FCSTD DOCUMENT  (FreeCAD 0.16RUnknown)
Label: 2d-box-spectro
License: All rights reserved
LicenseURL: http://en.wikipedia.org/wiki/All_rights_reserved
objects: Sketcher::SketchObject×6, Spreadsheet::Sheet×1
note: 6 computed .brp shape members not serialized (recipe doc carries the construction recipe); baked Part::Feature solids carry a one-line shape summary decoded from their .brp

FEATURE [Spreadsheet::Sheet] Spreadsheet  label="prefs"
  cells = A1=width; B1(width)==pcbLength + 2 * pcbSpace + 2 * thickness; C1=mm; A2=depth; B2(depth)==pcbWidth + 2 * pcbSpace + 2 * thickness; C2=mm; E2=surface; F2==width * depth * 3 + width * height * 2 + depth * height * 2; A3=height; B3(height)=32; C3=mm; A4=thickness; B4(thickness)=3; C4=mm; A5=space; B5(space)=5; C5=mm; D5=space between elements; A6=pcbLength; B6(pcbLength)=98.7; C6=mm; A7=pcbWidth; B7(pcbWidth)=73.2; C7=mm; A8=pcbSpace; B8(pcbSpace)=2; C8=mm; A9=supportX; B9(supportX)==pcbSpace + 3.5; C9=from box internal corner; A10=supportY; B10(supportY)==pcbSpace + 3.5; C10=from box internal corner; A11=supportRadius; B11(supportRadius)=1.5; A12=holeWidth; B12(holeWidth)=12.9; A13=holeX; B13(holeX)==48.7 + pcbSpace; C13=from box internal corner; A14=holeY; B14(holeY)==5.4 + pcbSpace; C14=from box internal corner; A15=screenLength; B15(screenLength)=71.59999999999999; A16=screenWidth; B16(screenWidth)=25.1; A17=screenX; B17(screenX)==pcbSpace + 13.4; C17=from box internal corner; A18=screenY; B18(screenY)==pcbSpace + 40.5; C18=from box internal corner; A19=rotaryX; B19(rotaryX)==pcbSpace + 13.2; A20=rotaryY; B20(rotaryY)==pcbSpace + 12.8; A21=rotaryRadius; B21(rotaryRadius)=4; A22=usbWidth; B22(usbWidth)=11; A23=usbHeight; B23(usbHeight)=9; A24=usbY; B24(usbY)==pcbSpace + 37.7; A25=usbZ; B25(usbZ)=6
FEATURE [Sketcher::SketchObject] Sketch  label="bottom"
  expr: Constraints[69] = prefs.supportY
  expr: Constraints[71] = prefs.supportY
  expr: Constraints[63] = prefs.supportRadius
  expr: Constraints[20] = prefs.depth - 2 * prefs.thickness
  expr: Constraints[70] = prefs.supportY
  expr: Constraints[22] = prefs.depth
  expr: Constraints[68] = prefs.supportY
  expr: Constraints[67] = prefs.supportX
  expr: Constraints[62] = prefs.supportRadius
  expr: Constraints[64] = prefs.supportX
  expr: Constraints[65] = prefs.supportX
  expr: Constraints[61] = prefs.supportRadius
  expr: Constraints[50] = prefs.width - 2 * prefs.thickness
  expr: Constraints[60] = prefs.supportRadius
  expr: Constraints[66] = prefs.supportX
  expr: Constraints[51] = prefs.width
  expr: Constraints[21] = prefs.depth - 2 * prefs.thickness
  sketch-geometry (25):
    g0: LineSegment StartX=3 StartY=80.2 StartZ=0 EndX=37.2333 EndY=80.2 EndZ=0
    g1: LineSegment StartX=37.2333 StartY=80.2 StartZ=0 EndX=37.2333 EndY=83.2 EndZ=0
    g2: LineSegment StartX=37.2333 StartY=83.2 StartZ=0 EndX=71.4667 EndY=83.2 EndZ=0
    g3: LineSegment StartX=71.4667 StartY=83.2 StartZ=0 EndX=71.4667 EndY=80.2 EndZ=0
    g4: LineSegment StartX=71.4667 StartY=80.2 StartZ=0 EndX=105.7 EndY=80.2 EndZ=0
    g5: LineSegment StartX=105.7 StartY=80.2 StartZ=0 EndX=105.7 EndY=54.4667 EndZ=0
    g6: LineSegment StartX=105.7 StartY=54.4667 StartZ=0 EndX=108.7 EndY=54.4667 EndZ=0
    g7: LineSegment StartX=108.7 StartY=54.4667 StartZ=0 EndX=108.7 EndY=28.7333 EndZ=0
    g8: LineSegment StartX=108.7 StartY=28.7333 StartZ=0 EndX=105.7 EndY=28.7333 EndZ=0
    g9: LineSegment StartX=105.7 StartY=28.7333 StartZ=0 EndX=105.7 EndY=3 EndZ=0
    g10: LineSegment StartX=105.7 StartY=3 StartZ=0 EndX=71.4667 EndY=3 EndZ=0
    g11: LineSegment StartX=71.4667 StartY=3 StartZ=0 EndX=71.4667 EndY=0 EndZ=0
    g12: LineSegment StartX=71.4667 StartY=0 StartZ=0 EndX=37.2333 EndY=0 EndZ=0
    g13: LineSegment StartX=37.2333 StartY=0 StartZ=0 EndX=37.2333 EndY=3 EndZ=0
    g14: LineSegment StartX=37.2333 StartY=3 StartZ=0 EndX=3 EndY=3 EndZ=0
    g15: LineSegment StartX=3 StartY=3 StartZ=0 EndX=3 EndY=28.7333 EndZ=0
    g16: LineSegment StartX=3 StartY=28.7333 StartZ=0 EndX=0 EndY=28.7333 EndZ=0
    g17: LineSegment StartX=0 StartY=28.7333 StartZ=0 EndX=0 EndY=54.4667 EndZ=0
    g18: LineSegment StartX=0 StartY=54.4667 StartZ=0 EndX=3 EndY=54.4667 EndZ=0
    g19: LineSegment StartX=3 StartY=54.4667 StartZ=0 EndX=3 EndY=80.2 EndZ=0
    g20: GeomPoint [constr] X=-41.8758 Y=-31.3252 Z=0
    g21: Circle CenterX=8.5 CenterY=74.7 CenterZ=0 NormalX=0 NormalY=0 NormalZ=1 Radius=1.5
    g22: Circle CenterX=100.2 CenterY=74.7 CenterZ=0 NormalX=0 NormalY=0 NormalZ=1 Radius=1.5
    g23: Circle CenterX=8.5 CenterY=8.5 CenterZ=0 NormalX=0 NormalY=0 NormalZ=1 Radius=1.5
    g24: Circle CenterX=100.2 CenterY=8.5 CenterZ=0 NormalX=0 NormalY=0 NormalZ=1 Radius=1.5
  constraints (72):
    c: Coincident(g0,g1)
    c: Coincident(g1,g2)
    c: Coincident(g2,g3)
    c: Coincident(g3,g4)
    c: Coincident(g4,g5)
    c: Coincident(g5,g6)
    c: Coincident(g6,g7)
    c: Coincident(g7,g8)
    c: Coincident(g8,g9)
    c: Coincident(g9,g10)
    c: Coincident(g10,g11)
    c: Coincident(g11,g12)
    c: Coincident(g12,g13)
    c: Coincident(g13,g14)
    c: Coincident(g14,g15)
    c: Coincident(g15,g16)
    c: Coincident(g16,g17)
    c: Coincident(g17,g18)
    c: Coincident(g18,g19)
    c: Coincident(g19,g0)
    c: DistanceY(g9,g4) = 77.2
    c: DistanceY(g14,g0) = 77.2
    c: DistanceY(g12,g1) = 83.2
    c: Horizontal(g0)
    c: Horizontal(g2)
    c: Horizontal(g4)
    c: Horizontal(g10)
    c: Horizontal(g12)
    c: Horizontal(g14)
    c: Equal(g1,g13)
    c: Equal(g0,g2)
    c: Equal(g2,g4)
    c: Equal(g4,g10)
    c: Equal(g10,g12)
    c: Equal(g12,g14)
    c: Equal(g3,g11)
    c: Equal(g5,g7)
    c: Equal(g7,g9)
    c: Equal(g9,g19)
    c: Equal(g19,g17)
    c: Equal(g17,g15)
    c: Vertical(g3)
    c: Vertical(g1)
    c: Vertical(g13)
    c: Vertical(g11)
    c: Horizontal(g18)
    c: Horizontal(g16)
    c: Horizontal(g8)
    c: Equal(g18,g6)
    c: Equal(g16,g8)
    c: DistanceX(g0,g4) = 102.7
    c: DistanceX(g16,g7) = 108.7
    c: Vertical(g15)
    c: Vertical(g19)
    c: Vertical(g17)
    c: Vertical(g5)
    c: Vertical(g7)
    c: Vertical(g9)
    c: DistanceX(g-1,g16) = 0
    c: DistanceY(g12,g-1) = 0
    c: Radius(g21) = 1.5
    c: Radius(g22) = 1.5
    c: Radius(g23) = 1.5
    c: Radius(g24) = 1.5
    c: DistanceX(g0,g21) = 5.5
    c: DistanceX(g22,g4) = 5.5
    c: DistanceX(g24,g9) = 5.5
    c: DistanceX(g14,g23) = 5.5
    c: DistanceY(g21,g0) = 5.5
    c: DistanceY(g22,g4) = 5.5
    c: DistanceY(g9,g24) = 5.5
    c: DistanceY(g14,g23) = 5.5
FEATURE [Sketcher::SketchObject] Sketch001  label="front"
  Placement = pos=(0,88.2,0) rot=(0,0,1;0rad)
  expr: Placement.Base.y = prefs.depth + Spreadsheet.space
  expr: Constraints[20] = prefs.height
  expr: Constraints[49] = prefs.width
  expr: Constraints[21] = prefs.height
  expr: Constraints[48] = prefs.width - 2 * prefs.thickness
  expr: Constraints[22] = prefs.height - 2 * prefs.thickness
  sketch-geometry (21):
    g0: LineSegment StartX=3 StartY=32 StartZ=0 EndX=37.2333 EndY=32 EndZ=0
    g1: LineSegment StartX=37.2333 StartY=32 StartZ=0 EndX=37.2333 EndY=29 EndZ=0
    g2: LineSegment StartX=37.2333 StartY=29 StartZ=0 EndX=71.4667 EndY=29 EndZ=0
    g3: LineSegment StartX=71.4667 StartY=29 StartZ=0 EndX=71.4667 EndY=32 EndZ=0
    g4: LineSegment StartX=71.4667 StartY=32 StartZ=0 EndX=105.7 EndY=32 EndZ=0
    g5: LineSegment StartX=105.7 StartY=32 StartZ=0 EndX=105.7 EndY=21.3333 EndZ=0
    g6: LineSegment StartX=105.7 StartY=21.3333 StartZ=0 EndX=108.7 EndY=21.3333 EndZ=0
    g7: LineSegment StartX=108.7 StartY=21.3333 StartZ=0 EndX=108.7 EndY=10.6667 EndZ=0
    g8: LineSegment StartX=108.7 StartY=10.6667 StartZ=0 EndX=105.7 EndY=10.6667 EndZ=0
    g9: LineSegment StartX=105.7 StartY=10.6667 StartZ=0 EndX=105.7 EndY=0 EndZ=0
    g10: LineSegment StartX=105.7 StartY=0 StartZ=0 EndX=71.4667 EndY=0 EndZ=0
    g11: LineSegment StartX=71.4667 StartY=0 StartZ=0 EndX=71.4667 EndY=3 EndZ=0
    g12: LineSegment StartX=71.4667 StartY=3 StartZ=0 EndX=37.2333 EndY=3 EndZ=0
    g13: LineSegment StartX=37.2333 StartY=3 StartZ=0 EndX=37.2333 EndY=0 EndZ=0
    g14: LineSegment StartX=37.2333 StartY=0 StartZ=0 EndX=3 EndY=0 EndZ=0
    g15: LineSegment StartX=3 StartY=0 StartZ=0 EndX=3 EndY=10.6667 EndZ=0
    g16: LineSegment StartX=3 StartY=10.6667 StartZ=0 EndX=0 EndY=10.6667 EndZ=0
    g17: LineSegment StartX=0 StartY=10.6667 StartZ=0 EndX=0 EndY=21.3333 EndZ=0
    g18: LineSegment StartX=0 StartY=21.3333 StartZ=0 EndX=3 EndY=21.3333 EndZ=0
    g19: LineSegment StartX=3 StartY=21.3333 StartZ=0 EndX=3 EndY=32 EndZ=0
    g20: GeomPoint [constr] X=-41.8758 Y=-31.3252 Z=0
  constraints (60):
    c: Coincident(g0,g1)
    c: Coincident(g1,g2)
    c: Coincident(g2,g3)
    c: Coincident(g3,g4)
    c: Coincident(g4,g5)
    c: Coincident(g5,g6)
    c: Coincident(g6,g7)
    c: Coincident(g7,g8)
    c: Coincident(g8,g9)
    c: Coincident(g9,g10)
    c: Coincident(g10,g11)
    c: Coincident(g11,g12)
    c: Coincident(g12,g13)
    c: Coincident(g13,g14)
    c: Coincident(g14,g15)
    c: Coincident(g15,g16)
    c: Coincident(g16,g17)
    c: Coincident(g17,g18)
    c: Coincident(g18,g19)
    c: Coincident(g19,g0)
    c: DistanceY(g9,g4) = 32
    c: DistanceY(g14,g0) = 32
    c: DistanceY(g12,g1) = 26
    c: Horizontal(g0)
    c: Horizontal(g2)
    c: Horizontal(g4)
    c: Horizontal(g10)
    c: Horizontal(g12)
    c: Horizontal(g14)
    c: Equal(g0,g2)
    c: Equal(g2,g4)
    c: Equal(g4,g10)
    c: Equal(g10,g12)
    c: Equal(g12,g14)
    c: Equal(g5,g7)
    c: Equal(g7,g9)
    c: Equal(g9,g19)
    c: Equal(g19,g17)
    c: Equal(g17,g15)
    c: Vertical(g3)
    c: Vertical(g1)
    c: Vertical(g13)
    c: Vertical(g11)
    c: Horizontal(g18)
    c: Horizontal(g16)
    c: Horizontal(g8)
    c: Equal(g18,g6)
    c: Equal(g16,g8)
    c: DistanceX(g0,g4) = 102.7
    c: DistanceX(g16,g7) = 108.7
    c: Vertical(g15)
    c: Vertical(g19)
    c: Vertical(g17)
    c: Vertical(g5)
    c: Vertical(g7)
    c: Vertical(g9)
    c: DistanceX(g-1,g16) = 0
    c: Equal(g1,g13)
    c: Equal(g3,g11)
    c: DistanceY(g-1,g14) = 0
FEATURE [Sketcher::SketchObject] Sketch002  label="left"
  Placement = pos=(0,125.2,0) rot=(0,0,1;0rad)
  expr: Constraints[59] = (prefs.depth - 2 * prefs.thickness) / 3
  expr: Constraints[53] = prefs.depth - 2 * prefs.thickness
  expr: Constraints[54] = prefs.depth
  expr: Placement.Base.y = prefs.depth + prefs.height + Spreadsheet.space * 2
  expr: Constraints[20] = prefs.height
  expr: Constraints[21] = prefs.height
  expr: Constraints[22] = prefs.height - 2 * prefs.thickness
  sketch-geometry (21):
    g0: LineSegment StartX=0 StartY=32 StartZ=0 EndX=28.7333 EndY=32 EndZ=0
    g1: LineSegment StartX=28.7333 StartY=32 StartZ=0 EndX=28.7333 EndY=29 EndZ=0
    g2: LineSegment StartX=28.7333 StartY=29 StartZ=0 EndX=54.4667 EndY=29 EndZ=0
    g3: LineSegment StartX=54.4667 StartY=29 StartZ=0 EndX=54.4667 EndY=32 EndZ=0
    g4: LineSegment StartX=54.4667 StartY=32 StartZ=0 EndX=83.2 EndY=32 EndZ=0
    g5: LineSegment StartX=83.2 StartY=32 StartZ=0 EndX=83.2 EndY=21.3333 EndZ=0
    g6: LineSegment StartX=83.2 StartY=21.3333 StartZ=0 EndX=80.2 EndY=21.3333 EndZ=0
    g7: LineSegment StartX=80.2 StartY=21.3333 StartZ=0 EndX=80.2 EndY=10.6667 EndZ=0
    g8: LineSegment StartX=80.2 StartY=10.6667 StartZ=0 EndX=83.2 EndY=10.6667 EndZ=0
    g9: LineSegment StartX=83.2 StartY=10.6667 StartZ=0 EndX=83.2 EndY=0 EndZ=0
    g10: LineSegment StartX=83.2 StartY=0 StartZ=0 EndX=54.4667 EndY=0 EndZ=0
    g11: LineSegment StartX=54.4667 StartY=0 StartZ=0 EndX=54.4667 EndY=3 EndZ=0
    g12: LineSegment StartX=54.4667 StartY=3 StartZ=0 EndX=28.7333 EndY=3 EndZ=0
    g13: LineSegment StartX=28.7333 StartY=3 StartZ=0 EndX=28.7333 EndY=0 EndZ=0
    g14: LineSegment StartX=28.7333 StartY=0 StartZ=0 EndX=0 EndY=0 EndZ=0
    g15: LineSegment StartX=0 StartY=0 StartZ=0 EndX=0 EndY=10.6667 EndZ=0
    g16: LineSegment StartX=0 StartY=10.6667 StartZ=0 EndX=3 EndY=10.6667 EndZ=0
    g17: LineSegment StartX=3 StartY=10.6667 StartZ=0 EndX=3 EndY=21.3333 EndZ=0
    g18: LineSegment StartX=3 StartY=21.3333 StartZ=0 EndX=0 EndY=21.3333 EndZ=0
    g19: LineSegment StartX=0 StartY=21.3333 StartZ=0 EndX=0 EndY=32 EndZ=0
    g20: GeomPoint [constr] X=-41.8758 Y=-31.3252 Z=0
  constraints (60):
    c: Coincident(g0,g1)
    c: Coincident(g1,g2)
    c: Coincident(g2,g3)
    c: Coincident(g3,g4)
    c: Coincident(g4,g5)
    c: Coincident(g5,g6)
    c: Coincident(g6,g7)
    c: Coincident(g7,g8)
    c: Coincident(g8,g9)
    c: Coincident(g9,g10)
    c: Coincident(g10,g11)
    c: Coincident(g11,g12)
    c: Coincident(g12,g13)
    c: Coincident(g13,g14)
    c: Coincident(g14,g15)
    c: Coincident(g15,g16)
    c: Coincident(g16,g17)
    c: Coincident(g17,g18)
    c: Coincident(g18,g19)
    c: Coincident(g19,g0)
    c: DistanceY(g9,g4) = 32
    c: DistanceY(g14,g0) = 32
    c: DistanceY(g12,g1) = 26
    c: Horizontal(g0)
    c: Horizontal(g2)
    c: Horizontal(g4)
    c: Horizontal(g10)
    c: Horizontal(g12)
    c: Horizontal(g14)
    c: Equal(g4,g10)
    c: Equal(g5,g7)
    c: Equal(g7,g9)
    c: Equal(g9,g19)
    c: Equal(g19,g17)
    c: Equal(g17,g15)
    c: Vertical(g3)
    c: Vertical(g1)
    c: Vertical(g13)
    c: Vertical(g11)
    c: Horizontal(g18)
    c: Horizontal(g16)
    c: Vertical(g15)
    c: Vertical(g19)
    c: Vertical(g17)
    c: Vertical(g5)
    c: Vertical(g7)
    c: Vertical(g9)
    c: Equal(g1,g13)
    c: Equal(g3,g11)
    c: DistanceY(g-1,g14) = 0
    c: Horizontal(g6)
    c: Equal(g18,g6)
    c: Equal(g16,g8)
    c: DistanceX(g17,g6) = 77.2
    c: DistanceX(g0,g4) = 83.2
    c: DistanceX(g-1,g14) = 0
    c: Equal(g14,g10)
    c: Equal(g0,g4)
    c: Equal(g2,g12)
    c: DistanceX(g2,g2) = 25.7333
FEATURE [Sketcher::SketchObject] Sketch003  label="top"
  Placement = pos=(113.7,0,0) rot=(0,0,1;0rad)
  expr: Constraints[87] = prefs.supportX
  expr: Constraints[79] = prefs.supportRadius
  expr: Constraints[93] = prefs.holeWidth
  expr: Constraints[92] = prefs.rotaryRadius
  expr: Constraints[77] = prefs.supportRadius
  expr: Constraints[98] = prefs.screenX
  expr: Constraints[95] = prefs.holeY
  expr: Constraints[89] = prefs.screenWidth
  expr: Constraints[84] = prefs.supportX
  expr: Constraints[76] = prefs.supportRadius
  expr: Constraints[22] = prefs.depth
  expr: Constraints[50] = prefs.width - 2 * prefs.thickness
  expr: Constraints[96] = prefs.holeX
  expr: Constraints[97] = prefs.rotaryX
  expr: Constraints[82] = prefs.supportX
  expr: Constraints[86] = prefs.supportY
  expr: Constraints[88] = prefs.screenLength
  expr: Placement.Base.x = prefs.width + Spreadsheet.space
  expr: Constraints[85] = prefs.supportY
  expr: Constraints[83] = prefs.supportY
  expr: Constraints[78] = prefs.supportRadius
  expr: Constraints[81] = prefs.supportY
  expr: Constraints[21] = prefs.depth - 2 * prefs.thickness
  expr: Constraints[51] = prefs.width
  expr: Constraints[20] = prefs.depth - 2 * prefs.thickness
  expr: Constraints[80] = prefs.supportX
  sketch-geometry (34):
    g0: LineSegment StartX=3 StartY=80.2 StartZ=0 EndX=37.2333 EndY=80.2 EndZ=0
    g1: LineSegment StartX=37.2333 StartY=80.2 StartZ=0 EndX=37.2333 EndY=83.2 EndZ=0
    g2: LineSegment StartX=37.2333 StartY=83.2 StartZ=0 EndX=71.4667 EndY=83.2 EndZ=0
    g3: LineSegment StartX=71.4667 StartY=83.2 StartZ=0 EndX=71.4667 EndY=80.2 EndZ=0
    g4: LineSegment StartX=71.4667 StartY=80.2 StartZ=0 EndX=105.7 EndY=80.2 EndZ=0
    g5: LineSegment StartX=105.7 StartY=80.2 StartZ=0 EndX=105.7 EndY=54.4667 EndZ=0
    g6: LineSegment StartX=105.7 StartY=54.4667 StartZ=0 EndX=108.7 EndY=54.4667 EndZ=0
    g7: LineSegment StartX=108.7 StartY=54.4667 StartZ=0 EndX=108.7 EndY=28.7333 EndZ=0
    g8: LineSegment StartX=108.7 StartY=28.7333 StartZ=0 EndX=105.7 EndY=28.7333 EndZ=0
    g9: LineSegment StartX=105.7 StartY=28.7333 StartZ=0 EndX=105.7 EndY=3 EndZ=0
    g10: LineSegment StartX=105.7 StartY=3 StartZ=0 EndX=71.4667 EndY=3 EndZ=0
    g11: LineSegment StartX=71.4667 StartY=3 StartZ=0 EndX=71.4667 EndY=0 EndZ=0
    g12: LineSegment StartX=71.4667 StartY=0 StartZ=0 EndX=37.2333 EndY=0 EndZ=0
    g13: LineSegment StartX=37.2333 StartY=0 StartZ=0 EndX=37.2333 EndY=3 EndZ=0
    g14: LineSegment StartX=37.2333 StartY=3 StartZ=0 EndX=3 EndY=3 EndZ=0
    g15: LineSegment StartX=3 StartY=3 StartZ=0 EndX=3 EndY=28.7333 EndZ=0
    g16: LineSegment StartX=3 StartY=28.7333 StartZ=0 EndX=0 EndY=28.7333 EndZ=0
    g17: LineSegment StartX=0 StartY=28.7333 StartZ=0 EndX=0 EndY=54.4667 EndZ=0
    g18: LineSegment StartX=0 StartY=54.4667 StartZ=0 EndX=3 EndY=54.4667 EndZ=0
    g19: LineSegment StartX=3 StartY=54.4667 StartZ=0 EndX=3 EndY=80.2 EndZ=0
    g20: GeomPoint [constr] X=-41.8758 Y=-31.3252 Z=0
    g21: LineSegment StartX=18.7 StartY=69.1 StartZ=0 EndX=90.3 EndY=69.1 EndZ=0
    g22: LineSegment StartX=90.3 StartY=69.1 StartZ=0 EndX=90.3 EndY=44 EndZ=0
    g23: LineSegment StartX=90.3 StartY=44 StartZ=0 EndX=18.7 EndY=44 EndZ=0
    g24: LineSegment StartX=18.7 StartY=44 StartZ=0 EndX=18.7 EndY=69.1 EndZ=0
    g25: Circle CenterX=90.5 CenterY=16.3 CenterZ=0 NormalX=0 NormalY=0 NormalZ=1 Radius=4
    g26: Circle CenterX=8.5 CenterY=74.7 CenterZ=0 NormalX=0 NormalY=0 NormalZ=1 Radius=1.5
    g27: Circle CenterX=100.2 CenterY=74.7 CenterZ=0 NormalX=0 NormalY=0 NormalZ=1 Radius=1.5
    g28: Circle CenterX=8.5 CenterY=8.5 CenterZ=0 NormalX=0 NormalY=0 NormalZ=1 Radius=1.5
    g29: Circle CenterX=100.2 CenterY=8.5 CenterZ=0 NormalX=0 NormalY=0 NormalZ=1 Radius=1.5
    g30: LineSegment StartX=42.1 StartY=23.3 StartZ=0 EndX=55 EndY=23.3 EndZ=0
    g31: LineSegment StartX=55 StartY=23.3 StartZ=0 EndX=55 EndY=10.4 EndZ=0
    g32: LineSegment StartX=55 StartY=10.4 StartZ=0 EndX=42.1 EndY=10.4 EndZ=0
    g33: LineSegment StartX=42.1 StartY=10.4 StartZ=0 EndX=42.1 EndY=23.3 EndZ=0
  constraints (99):
    c: Coincident(g0,g1)
    c: Coincident(g1,g2)
    c: Coincident(g2,g3)
    c: Coincident(g3,g4)
    c: Coincident(g4,g5)
    c: Coincident(g5,g6)
    c: Coincident(g6,g7)
    c: Coincident(g7,g8)
    c: Coincident(g8,g9)
    c: Coincident(g9,g10)
    c: Coincident(g10,g11)
    c: Coincident(g11,g12)
    c: Coincident(g12,g13)
    c: Coincident(g13,g14)
    c: Coincident(g14,g15)
    c: Coincident(g15,g16)
    c: Coincident(g16,g17)
    c: Coincident(g17,g18)
    c: Coincident(g18,g19)
    c: Coincident(g19,g0)
    c: DistanceY(g9,g4) = 77.2
    c: DistanceY(g14,g0) = 77.2
    c: DistanceY(g12,g1) = 83.2
    c: Horizontal(g0)
    c: Horizontal(g2)
    c: Horizontal(g4)
    c: Horizontal(g10)
    c: Horizontal(g12)
    c: Horizontal(g14)
    c: Equal(g1,g13)
    c: Equal(g0,g2)
    c: Equal(g2,g4)
    c: Equal(g4,g10)
    c: Equal(g10,g12)
    c: Equal(g12,g14)
    c: Equal(g3,g11)
    c: Equal(g5,g7)
    c: Equal(g7,g9)
    c: Equal(g9,g19)
    c: Equal(g19,g17)
    c: Equal(g17,g15)
    c: Vertical(g3)
    c: Vertical(g1)
    c: Vertical(g13)
    c: Vertical(g11)
    c: Horizontal(g18)
    c: Horizontal(g16)
    c: Horizontal(g8)
    c: Equal(g18,g6)
    c: Equal(g16,g8)
    c: DistanceX(g0,g4) = 102.7
    c: DistanceX(g16,g7) = 108.7
    c: Vertical(g15)
    c: Vertical(g19)
    c: Vertical(g17)
    c: Vertical(g5)
    c: Vertical(g7)
    c: Vertical(g9)
    c: DistanceX(g-1,g16) = 0
    c: DistanceY(g12,g-1) = 0
    c: Coincident(g21,g22)
    c: Coincident(g22,g23)
    c: Coincident(g23,g24)
    c: Coincident(g24,g21)
    c: Horizontal(g21)
    c: Horizontal(g23)
    c: Vertical(g22)
    c: Vertical(g24)
    c: Coincident(g30,g31)
    c: Coincident(g31,g32)
    c: Coincident(g32,g33)
    c: Coincident(g33,g30)
    c: Horizontal(g30)
    c: Horizontal(g32)
    c: Vertical(g31)
    c: Vertical(g33)
    c: Radius(g26) = 1.5
    c: Radius(g28) = 1.5
    c: Radius(g27) = 1.5
    c: Radius(g29) = 1.5
    c: DistanceX(g0,g26) = 5.5
    c: DistanceY(g26,g0) = 5.5
    c: DistanceX(g27,g4) = 5.5
    c: DistanceY(g27,g4) = 5.5
    c: DistanceX(g29,g9) = 5.5
    c: DistanceY(g9,g29) = 5.5
    c: DistanceY(g14,g28) = 5.5
    c: DistanceX(g14,g28) = 5.5
    c: DistanceX(g23,g22) = 71.6
    c: DistanceY(g22,g21) = 25.1
    c: DistanceY(g14,g23) = 41
    c: DistanceY(g14,g25) = 13.3
    c: Radius(g25) = 4
    c: DistanceX(g30,g30) = 12.9
    c: Equal(g30,g31)
    c: DistanceY(g14,g32) = 7.4
    c: DistanceX(g31,g9) = 50.7
    c: DistanceX(g25,g9) = 15.2
    c: DistanceX(g22,g9) = 15.4
FEATURE [Sketcher::SketchObject] Sketch004  label="back"
  Placement = pos=(113.7,88.2,0) rot=(0,0,1;0rad)
  expr: Placement.Base.x = prefs.width + Spreadsheet.space
  expr: Placement.Base.y = prefs.depth + Spreadsheet.space
  expr: Constraints[20] = prefs.height
  expr: Constraints[49] = prefs.width
  expr: Constraints[21] = prefs.height
  expr: Constraints[48] = prefs.width - 2 * prefs.thickness
  expr: Constraints[22] = prefs.height - 2 * prefs.thickness
  sketch-geometry (21):
    g0: LineSegment StartX=3 StartY=32 StartZ=0 EndX=37.2333 EndY=32 EndZ=0
    g1: LineSegment StartX=37.2333 StartY=32 StartZ=0 EndX=37.2333 EndY=29 EndZ=0
    g2: LineSegment StartX=37.2333 StartY=29 StartZ=0 EndX=71.4667 EndY=29 EndZ=0
    g3: LineSegment StartX=71.4667 StartY=29 StartZ=0 EndX=71.4667 EndY=32 EndZ=0
    g4: LineSegment StartX=71.4667 StartY=32 StartZ=0 EndX=105.7 EndY=32 EndZ=0
    g5: LineSegment StartX=105.7 StartY=32 StartZ=0 EndX=105.7 EndY=21.3333 EndZ=0
    g6: LineSegment StartX=105.7 StartY=21.3333 StartZ=0 EndX=108.7 EndY=21.3333 EndZ=0
    g7: LineSegment StartX=108.7 StartY=21.3333 StartZ=0 EndX=108.7 EndY=10.6667 EndZ=0
    g8: LineSegment StartX=108.7 StartY=10.6667 StartZ=0 EndX=105.7 EndY=10.6667 EndZ=0
    g9: LineSegment StartX=105.7 StartY=10.6667 StartZ=0 EndX=105.7 EndY=0 EndZ=0
    g10: LineSegment StartX=105.7 StartY=0 StartZ=0 EndX=71.4667 EndY=0 EndZ=0
    g11: LineSegment StartX=71.4667 StartY=0 StartZ=0 EndX=71.4667 EndY=3 EndZ=0
    g12: LineSegment StartX=71.4667 StartY=3 StartZ=0 EndX=37.2333 EndY=3 EndZ=0
    g13: LineSegment StartX=37.2333 StartY=3 StartZ=0 EndX=37.2333 EndY=0 EndZ=0
    g14: LineSegment StartX=37.2333 StartY=0 StartZ=0 EndX=3 EndY=0 EndZ=0
    g15: LineSegment StartX=3 StartY=0 StartZ=0 EndX=3 EndY=10.6667 EndZ=0
    g16: LineSegment StartX=3 StartY=10.6667 StartZ=0 EndX=0 EndY=10.6667 EndZ=0
    g17: LineSegment StartX=0 StartY=10.6667 StartZ=0 EndX=0 EndY=21.3333 EndZ=0
    g18: LineSegment StartX=0 StartY=21.3333 StartZ=0 EndX=3 EndY=21.3333 EndZ=0
    g19: LineSegment StartX=3 StartY=21.3333 StartZ=0 EndX=3 EndY=32 EndZ=0
    g20: GeomPoint [constr] X=-41.8758 Y=-31.3252 Z=0
  constraints (60):
    c: Coincident(g0,g1)
    c: Coincident(g1,g2)
    c: Coincident(g2,g3)
    c: Coincident(g3,g4)
    c: Coincident(g4,g5)
    c: Coincident(g5,g6)
    c: Coincident(g6,g7)
    c: Coincident(g7,g8)
    c: Coincident(g8,g9)
    c: Coincident(g9,g10)
    c: Coincident(g10,g11)
    c: Coincident(g11,g12)
    c: Coincident(g12,g13)
    c: Coincident(g13,g14)
    c: Coincident(g14,g15)
    c: Coincident(g15,g16)
    c: Coincident(g16,g17)
    c: Coincident(g17,g18)
    c: Coincident(g18,g19)
    c: Coincident(g19,g0)
    c: DistanceY(g9,g4) = 32
    c: DistanceY(g14,g0) = 32
    c: DistanceY(g12,g1) = 26
    c: Horizontal(g0)
    c: Horizontal(g2)
    c: Horizontal(g4)
    c: Horizontal(g10)
    c: Horizontal(g12)
    c: Horizontal(g14)
    c: Equal(g0,g2)
    c: Equal(g2,g4)
    c: Equal(g4,g10)
    c: Equal(g10,g12)
    c: Equal(g12,g14)
    c: Equal(g5,g7)
    c: Equal(g7,g9)
    c: Equal(g9,g19)
    c: Equal(g19,g17)
    c: Equal(g17,g15)
    c: Vertical(g3)
    c: Vertical(g1)
    c: Vertical(g13)
    c: Vertical(g11)
    c: Horizontal(g18)
    c: Horizontal(g16)
    c: Horizontal(g8)
    c: Equal(g18,g6)
    c: Equal(g16,g8)
    c: DistanceX(g0,g4) = 102.7
    c: DistanceX(g16,g7) = 108.7
    c: Vertical(g15)
    c: Vertical(g19)
    c: Vertical(g17)
    c: Vertical(g5)
    c: Vertical(g7)
    c: Vertical(g9)
    c: DistanceX(g-1,g16) = 0
    c: Equal(g1,g13)
    c: Equal(g3,g11)
    c: DistanceY(g-1,g14) = 0
FEATURE [Sketcher::SketchObject] Sketch006  label="right"
  Placement = pos=(88.2,125.2,0) rot=(0,0,1;0rad)
  expr: Constraints[68] = prefs.usbWidth
  expr: Placement.Base.x = prefs.depth + Spreadsheet.space
  expr: Placement.Base.y = prefs.depth + prefs.height + Spreadsheet.space * 2
  expr: Constraints[20] = prefs.height
  expr: Constraints[71] = prefs.usbZ
  expr: Constraints[69] = prefs.usbHeight
  expr: Constraints[21] = prefs.height
  expr: Constraints[59] = (prefs.depth - 2 * prefs.thickness) / 3
  expr: Constraints[53] = prefs.depth - 2 * prefs.thickness
  expr: Constraints[54] = prefs.depth
  expr: Constraints[70] = prefs.usbY
  expr: Constraints[22] = prefs.height - 2 * prefs.thickness
  sketch-geometry (25):
    g0: LineSegment StartX=0 StartY=32 StartZ=0 EndX=28.7333 EndY=32 EndZ=0
    g1: LineSegment StartX=28.7333 StartY=32 StartZ=0 EndX=28.7333 EndY=29 EndZ=0
    g2: LineSegment StartX=28.7333 StartY=29 StartZ=0 EndX=54.4667 EndY=29 EndZ=0
    g3: LineSegment StartX=54.4667 StartY=29 StartZ=0 EndX=54.4667 EndY=32 EndZ=0
    g4: LineSegment StartX=54.4667 StartY=32 StartZ=0 EndX=83.2 EndY=32 EndZ=0
    g5: LineSegment StartX=83.2 StartY=32 StartZ=0 EndX=83.2 EndY=21.3333 EndZ=0
    g6: LineSegment StartX=83.2 StartY=21.3333 StartZ=0 EndX=80.2 EndY=21.3333 EndZ=0
    g7: LineSegment StartX=80.2 StartY=21.3333 StartZ=0 EndX=80.2 EndY=10.6667 EndZ=0
    g8: LineSegment StartX=80.2 StartY=10.6667 StartZ=0 EndX=83.2 EndY=10.6667 EndZ=0
    g9: LineSegment StartX=83.2 StartY=10.6667 StartZ=0 EndX=83.2 EndY=0 EndZ=0
    g10: LineSegment StartX=83.2 StartY=0 StartZ=0 EndX=54.4667 EndY=0 EndZ=0
    g11: LineSegment StartX=54.4667 StartY=0 StartZ=0 EndX=54.4667 EndY=3 EndZ=0
    g12: LineSegment StartX=54.4667 StartY=3 StartZ=0 EndX=28.7333 EndY=3 EndZ=0
    g13: LineSegment StartX=28.7333 StartY=3 StartZ=0 EndX=28.7333 EndY=0 EndZ=0
    g14: LineSegment StartX=28.7333 StartY=0 StartZ=0 EndX=0 EndY=0 EndZ=0
    g15: LineSegment StartX=0 StartY=0 StartZ=0 EndX=0 EndY=10.6667 EndZ=0
    g16: LineSegment StartX=0 StartY=10.6667 StartZ=0 EndX=3 EndY=10.6667 EndZ=0
    g17: LineSegment StartX=3 StartY=10.6667 StartZ=0 EndX=3 EndY=21.3333 EndZ=0
    g18: LineSegment StartX=3 StartY=21.3333 StartZ=0 EndX=0 EndY=21.3333 EndZ=0
    g19: LineSegment StartX=0 StartY=21.3333 StartZ=0 EndX=0 EndY=32 EndZ=0
    g20: GeomPoint [constr] X=-41.8758 Y=-31.3252 Z=0
    g21: LineSegment StartX=29.5 StartY=23 StartZ=0 EndX=40.5 EndY=23 EndZ=0
    g22: LineSegment StartX=40.5 StartY=23 StartZ=0 EndX=40.5 EndY=14 EndZ=0
    g23: LineSegment StartX=40.5 StartY=14 StartZ=0 EndX=29.5 EndY=14 EndZ=0
    g24: LineSegment StartX=29.5 StartY=14 StartZ=0 EndX=29.5 EndY=23 EndZ=0
  constraints (72):
    c: Coincident(g0,g1)
    c: Coincident(g1,g2)
    c: Coincident(g2,g3)
    c: Coincident(g3,g4)
    c: Coincident(g4,g5)
    c: Coincident(g5,g6)
    c: Coincident(g6,g7)
    c: Coincident(g7,g8)
    c: Coincident(g8,g9)
    c: Coincident(g9,g10)
    c: Coincident(g10,g11)
    c: Coincident(g11,g12)
    c: Coincident(g12,g13)
    c: Coincident(g13,g14)
    c: Coincident(g14,g15)
    c: Coincident(g15,g16)
    c: Coincident(g16,g17)
    c: Coincident(g17,g18)
    c: Coincident(g18,g19)
    c: Coincident(g19,g0)
    c: DistanceY(g9,g4) = 32
    c: DistanceY(g14,g0) = 32
    c: DistanceY(g12,g1) = 26
    c: Horizontal(g0)
    c: Horizontal(g2)
    c: Horizontal(g4)
    c: Horizontal(g10)
    c: Horizontal(g12)
    c: Horizontal(g14)
    c: Equal(g4,g10)
    c: Equal(g5,g7)
    c: Equal(g7,g9)
    c: Equal(g9,g19)
    c: Equal(g19,g17)
    c: Equal(g17,g15)
    c: Vertical(g3)
    c: Vertical(g1)
    c: Vertical(g13)
    c: Vertical(g11)
    c: Horizontal(g18)
    c: Horizontal(g16)
    c: Vertical(g15)
    c: Vertical(g19)
    c: Vertical(g17)
    c: Vertical(g5)
    c: Vertical(g7)
    c: Vertical(g9)
    c: Equal(g1,g13)
    c: Equal(g3,g11)
    c: DistanceY(g-1,g14) = 0
    c: Horizontal(g6)
    c: Equal(g18,g6)
    c: Equal(g16,g8)
    c: DistanceX(g17,g6) = 77.2
    c: DistanceX(g0,g4) = 83.2
    c: DistanceX(g-1,g14) = 0
    c: Equal(g14,g10)
    c: Equal(g0,g4)
    c: Equal(g2,g12)
    c: DistanceX(g2,g2) = 25.7333
    c: Coincident(g21,g22)
    c: Coincident(g22,g23)
    c: Coincident(g23,g24)
    c: Coincident(g24,g21)
    c: Horizontal(g21)
    c: Horizontal(g23)
    c: Vertical(g22)
    c: Vertical(g24)
    c: DistanceX(g21,g21) = 11
    c: DistanceY(g22,g21) = 9
    c: DistanceX(g22,g7) = 39.7
    c: DistanceY(g21,g1) = 6
